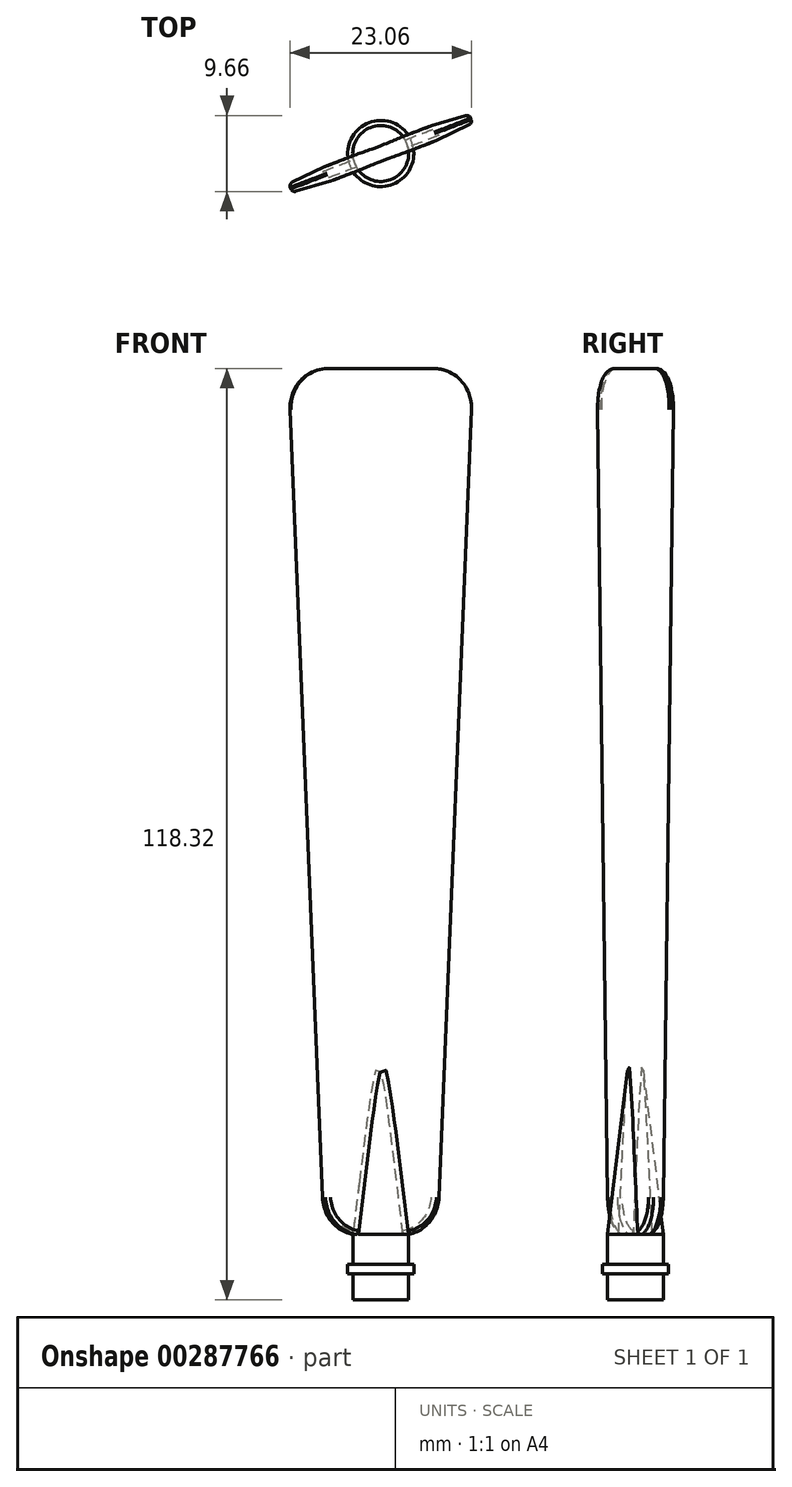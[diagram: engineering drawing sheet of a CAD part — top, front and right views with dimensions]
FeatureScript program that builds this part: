
annotation { "Feature Type Name" : "Feature", "Feature Type Description" : "" }
export const myFeature = defineFeature(function(context is Context, id is Id, definition is map)
    precondition{}
    {
        {
            var Q0;
            Q0=qCreatedBy(makeId("Top.planeOp"),FACE);
            var sketch = newSketch(context, id + "F0", { "sketchPlane" : qUnion([Q0])});
            skCircle(sketch, "E0", {"center": v(0, 0) * mm, "radius": 3.55 * mm});
            skSolve(sketch);
        }
        {
            var Q0;
            Q0=qCreatedBy(makeId("Top.planeOp"),FACE);
            cPlane(context, id + "F1", {"entities" : qUnion([Q0]), "cplaneType" : CPlaneType.OFFSET, "offset" : 10 * mm, "width" : 150 * mm, "height" : 150 * mm});
        }
        {
            var Q0;
            Q0=qCreatedBy(makeId("Top.planeOp"),FACE);
            cPlane(context, id + "F2", {"entities" : qUnion([Q0]), "cplaneType" : CPlaneType.OFFSET, "offset" : 120 * mm, "width" : 150 * mm, "height" : 150 * mm});
        }
        {
            var Q0;
            Q0=qCreatedBy(id+"F1.planeOp",FACE);
            var sketch = newSketch(context, id + "F3", { "sketchPlane" : qUnion([Q0])});
            skLineSegment(sketch, "E1", {"start": v(-7.36, -1.75) * mm, "end": v(6.64, 3.62) * mm});
            skLineSegment(sketch, "E2", {"start": v(6.64, 3.62) * mm, "end": v(7.36, 1.75) * mm});
            skLineSegment(sketch, "E3", {"start": v(7.36, 1.75) * mm, "end": v(-6.64, -3.62) * mm});
            skLineSegment(sketch, "E4", {"start": v(-6.64, -3.62) * mm, "end": v(-7.36, -1.75) * mm});
            skLineSegment(sketch, "E5", {"start": v(12.83, 4.92) * mm, "end": v(-12.36, -4.74) * mm, "construction": true});
            skLineSegment(sketch, "E6", {"start": v(-1.52, 3.95) * mm, "end": v(1.89, -4.92) * mm, "construction": true});
            skSolve(sketch);
        }
        {
            var Q0;
            Q0=qCreatedBy(id+"F2.planeOp",FACE);
            var sketch = newSketch(context, id + "F4", { "sketchPlane" : qUnion([Q0])});
            skLineSegment(sketch, "E7", {"start": v(-11.45, -5.04) * mm, "end": v(11.88, 3.92) * mm});
            skLineSegment(sketch, "E8", {"start": v(11.45, 5.04) * mm, "end": v(11.88, 3.92) * mm});
            skLineSegment(sketch, "E9", {"start": v(11.45, 5.04) * mm, "end": v(-11.88, -3.92) * mm});
            skLineSegment(sketch, "E10", {"start": v(-11.45, -5.04) * mm, "end": v(-11.88, -3.92) * mm});
            skLineSegment(sketch, "E11", {"start": v(-9.11, -3.5) * mm, "end": v(13.06, 5.01) * mm, "construction": true});
            skLineSegment(sketch, "E12", {"start": v(-1.12, 2.92) * mm, "end": v(1.55, -4.03) * mm, "construction": true});
            skSolve(sketch);
        }
        {
            var Q0;
            Q0=makeQuery(id+"F3.imprint","IMPRINT",FACE,{"disambiguationData":[TD([[makeQuery(id+"F3.imprint","IMPRINT",EDGE,{"derivedFrom":sQuery(id+"F3.wireOp",EDGE,"E1")}),-1.0]])]});
            var Q1;
            Q1=makeQuery(id+"F4.imprint","IMPRINT",FACE,{"disambiguationData":[TD([[makeQuery(id+"F4.imprint","IMPRINT",EDGE,{"derivedFrom":sQuery(id+"F4.wireOp",EDGE,"E7")}),1.0]])]});
            loft(context, id + "F5", {"sheetProfilesArray" : [{ "sheetProfileEntities" : qUnion([Q0]) }, { "sheetProfileEntities" : qUnion([Q1]) }]});
        }
        {
            var Q0;
            Q0=makeQuery(id+"F0.imprint","IMPRINT",FACE,{"disambiguationData":[TD([[makeQuery(id+"F0.imprint","IMPRINT",EDGE,{"derivedFrom":sQuery(id+"F0.wireOp",EDGE,"E0")}),1.0]])]});
            var Q1;
            Q1=makeQuery(id+"F5.opLoft","CAP_FACE",FACE,{"disambiguationData":[OSD([makeQuery(id+"F3.imprint","IMPRINT",FACE,{"disambiguationData":[TD([[makeQuery(id+"F3.imprint","IMPRINT",EDGE,{"derivedFrom":sQuery(id+"F3.wireOp",EDGE,"E1")}),-1.0]])]})])],"isStart":true});
            extrude(context, id + "F6", {"entities" : qUnion([Q0]), "operationType" : NewBodyOperationType.ADD, "endBound" : BoundingType.UP_TO_SURFACE, "endBoundEntityFace" : qUnion([Q1]), "offsetDistance" : 25 * mm, "depth" : 25 * mm});
        }
        {
            var Q0;
            Q0=makeQuery(id+"F5.opLoft","MID_CAP_EDGE",EDGE,{"disambiguationData":[OSD([sQuery(id+"F4.wireOp",EDGE,"E7"),sQuery(id+"F4.wireOp",EDGE,"E8"),sQuery(id+"F4.wireOp",EDGE,"E9")])],"capPos":1.0});
            var Q1;
            Q1=makeQuery(id+"F5.opLoft","MID_CAP_EDGE",EDGE,{"disambiguationData":[OSD([sQuery(id+"F4.wireOp",EDGE,"E7"),sQuery(id+"F4.wireOp",EDGE,"E9"),sQuery(id+"F4.wireOp",EDGE,"E10")])],"capPos":1.0});
            var Q2;
            Q2=makeQuery(id+"F5.opLoft","MID_CAP_EDGE",EDGE,{"disambiguationData":[OSD([sQuery(id+"F3.wireOp",EDGE,"E1"),sQuery(id+"F3.wireOp",EDGE,"E2"),sQuery(id+"F3.wireOp",EDGE,"E3")])],"capPos":0.0});
            var Q3;
            Q3=makeQuery(id+"F5.opLoft","MID_CAP_EDGE",EDGE,{"disambiguationData":[OSD([sQuery(id+"F3.wireOp",EDGE,"E1"),sQuery(id+"F3.wireOp",EDGE,"E3"),sQuery(id+"F3.wireOp",EDGE,"E4")])],"capPos":0.0});
            fillet(context, id + "F7", {"entities" : qUnion([Q0, Q1, Q2, Q3]), "radius" : 5 * mm, "tangentPropagation" : true, "allowEdgeOverflow" : false});
        }
        {
            var Q0;
            Q0=makeQuery(id+"F5.opLoft","SWEPT_EDGE",EDGE,{"disambiguationData":[OSD([sQuery(id+"F3.wireOp",EDGE,"E1"),sQuery(id+"F3.wireOp",EDGE,"E4"),sQuery(id+"F4.wireOp",EDGE,"E9"),sQuery(id+"F4.wireOp",EDGE,"E10")])]});
            var Q1;
            Q1=makeQuery(id+"F5.opLoft","SWEPT_EDGE",EDGE,{"disambiguationData":[OSD([sQuery(id+"F3.wireOp",EDGE,"E3"),sQuery(id+"F3.wireOp",EDGE,"E4"),sQuery(id+"F4.wireOp",EDGE,"E7"),sQuery(id+"F4.wireOp",EDGE,"E10")])]});
            fillet(context, id + "F8", {"entities" : qUnion([Q0, Q1]), "radius" : 0.5 * mm, "tangentPropagation" : true, "allowEdgeOverflow" : false});
        }
        {
            var Q0;
            Q0=qCreatedBy(makeId("Top.planeOp"),FACE);
            cPlane(context, id + "F9", {"entities" : qUnion([Q0]), "cplaneType" : CPlaneType.OFFSET, "offset" : 5 * mm, "width" : 150 * mm, "height" : 150 * mm});
        }
        {
            var Q0;
            Q0=qCreatedBy(id+"F9.planeOp",FACE);
            var sketch = newSketch(context, id + "F10", { "sketchPlane" : qUnion([Q0])});
            skCircle(sketch, "E13", {"center": v(0, 0) * mm, "radius": 4.2 * mm});
            skSolve(sketch);
        }
        {
            var Q0;
            Q0 = qSketchRegion(id + "F10", true);
            extrude(context, id + "F11", {"entities" : qUnion([Q0]), "operationType" : NewBodyOperationType.ADD, "depth" : 1.2 * mm});
        }
        {
            var Q0;
            {var subQ0=sQuery(id+"F3.wireOp",EDGE,"E4");var subQ1=sQuery(id+"F3.wireOp",EDGE,"E3");var subQ2=sQuery(id+"F3.wireOp",EDGE,"E2");var subQ3=sQuery(id+"F0.wireOp",EDGE,"E0");Q0=makeQuery(id+"F6.boolean.opBoolean","SPLIT",FACE,{"disambiguationData":[TD([makeQuery(id+"F5.opLoft","SWEPT_FACE",FACE,{"disambiguationData":[OSD([subQ2,subQ1,subQ0,sQuery(id+"F4.wireOp",EDGE,"E7"),sQuery(id+"F4.wireOp",EDGE,"E8"),sQuery(id+"F4.wireOp",EDGE,"E10")])]})])],"derivedFrom":makeQuery(id+"F6.opExtrude","CAP_FACE",FACE,{"disambiguationData":[OSD([subQ3])],"isStart":false})});}
            var sketch = newSketch(context, id + "F12", { "sketchPlane" : qUnion([Q0])});
            skCircle(sketch, "E14", {"center": v(0, 0) * mm, "radius": 3.55 * mm});
            skSolve(sketch);
        }
        {
            var Q0;
            Q0 = qSketchRegion(id + "F12", true);
            extrude(context, id + "F13", {"entities" : qUnion([Q0]), "operationType" : NewBodyOperationType.ADD, "depth" : 25 * mm, "offsetDistance" : 25 * mm, "hasDraft" : true, "draftAngle" : 7 * degree, "draftPullDirection" : true});
        }
        {
            var Q0;
            Q0=qCreatedBy(makeId("Front.planeOp"),FACE);
            var sketch = newSketch(context, id + "F14", { "sketchPlane" : qUnion([Q0])});
            skLineSegment(sketch, "E15.bottom", {"start": v(6.48, 1.68) * mm, "end": v(-6.1, 1.68) * mm});
            skLineSegment(sketch, "E15.top", {"start": v(6.48, -2.84) * mm, "end": v(-6.1, -2.84) * mm});
            skLineSegment(sketch, "E15.left", {"start": v(6.48, 1.68) * mm, "end": v(6.48, -2.84) * mm});
            skLineSegment(sketch, "E15.right", {"start": v(-6.1, 1.68) * mm, "end": v(-6.1, -2.84) * mm});
            skSolve(sketch);
        }
        {
            var Q0;
            Q0=makeQuery(id+"F14.imprint","IMPRINT",FACE,{"disambiguationData":[TD([[makeQuery(id+"F14.imprint","IMPRINT",EDGE,{"derivedFrom":sQuery(id+"F14.wireOp",EDGE,"E15.bottom")}),1.0]])]});
            extrude(context, id + "F15", {"entities" : qUnion([Q0]), "operationType" : NewBodyOperationType.REMOVE, "endBound" : BoundingType.SYMMETRIC, "oppositeDirection" : true, "depth" : 25 * mm, "offsetDistance" : 25 * mm});
        }
    });
